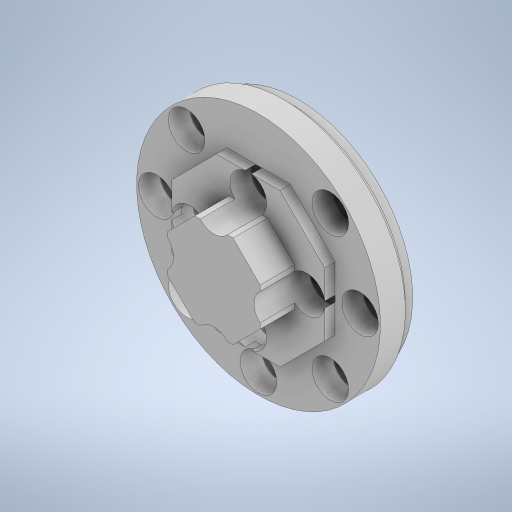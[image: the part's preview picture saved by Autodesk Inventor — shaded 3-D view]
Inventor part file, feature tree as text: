
AUTODESK INVENTOR PART (.ipt)
format: ipt  version: 2023.4 (Build 274418000, 418)  size: 473,600 bytes
history: native  units: mm
features: extrude x13, sketch x4, chamfer x3, projected_geometry x1
ambient origin geometry x8: Origin, YZ Plane, XZ Plane, XY Plane, X Axis, Y Axis, Z Axis, Center Point
bodies: Solid1 (feature_tree)
feature tree (21):
  extrude  "Extrusion1"  Depth=3.0mm TaperAngle=0.0deg
  extrude  "Extrusion2"  TaperAngle=0.0deg  [1 undecoded]
  chamfer  "Chamfer1"  Distance=2.0mm Angle=45.0deg
  extrude  "Extrusion3"  Depth=7.8mm TaperAngle=0.0deg
  extrude  "Extrusion4"  Depth=10.0mm TaperAngle=0.0deg
  extrude  "Extrusion5"  Depth=10.0mm
  extrude  "Extrusion6"  Depth=2.0mm TaperAngle=0.0deg
  extrude  "Extrusion7"  Depth=4.8mm TaperAngle=0.0deg
  extrude  "Extrusion8"  Depth=10.0mm
  chamfer  "Chamfer2"  Distance=4.0mm
  chamfer  "Chamfer3"  Distance=4.0mm
  extrude  "Extrusion9"  Depth=10.0mm
  extrude  "Extrusion10"  Depth=10.0mm
  extrude  "Extrusion11"  Depth=10.0mm
  extrude  "Extrusion12"  Depth=10.0mm
  extrude  "Extrusion13"  Depth=10.0mm
  sketch  "Sketch3"  dims[d0=45.1mm d1=3.0mm d2=0.0mm]
  projected_geometry  "Projected Loop1"
  sketch  "Sketch6"  dims[d3=29.0mm d4=0.0mm d5=0.0mm d6=0.5mm d7=2.0mm d8=45.0deg]
  sketch  "Sketch9"  dims[d9=0.05mm d10=7.8mm d11=0.0mm]
  sketch  "Sketch15"  dims[d12=12.0mm d13=0.0mm d14=2.8mm d15=0.0mm d16=0.05mm d17=2.0mm d18=0.0mm d19=4.8mm d20=0.0mm d21=48.0mm d22=4.0mm d23=4.0mm d24=4.0mm d25=4.0mm d26=4.0mm d27=4.0mm d28=4.0mm d29=10.9mm d30=4.8mm d31=0.0mm d32=1.1mm d33=2.0mm d34=45.0deg d35=0.2mm d36=2.0mm d37=45.0deg d38=23.0mm d39=4.0mm d40=40.0mm d42=360.0deg d44=0.0mm d45=0.0mm d46=7.2mm d47=40.0mm d49=360.0deg d51=8.4mm d52=0.0mm d53=7.2mm d54=80.0mm d56=360.0deg d58=4.2mm d59=0.0mm d60=10.0mm d61=0.0mm d62=10.0mm d63=0.0mm]
note: 1 required parameter value undecoded (feature->parameter linkage not recoverable at this tier; creation-order binding heuristic only, values carry confidence <= 0.55)
